# Revit family: Sanaa Basin 45cm PP
name_source: partatom
category: Plumbing Fixtures
units: mm (PartAtom-declared; Revit-internal decimal feet)

## family parameters
Always vertical = Yes
Cut with Voids When Loaded = No
Enable Cutting in Views = No
Maintain Annotation Orientation = No
OmniClass Number = 23.45.05.14.99
OmniClass Title = Other Sanitary Washing Plumbing Fixtures
Part Type = Normal
Room Calculation Point = No
Round Connector Dimension = Use Diameter
Shared = No
Work Plane-Based = No

## types (1)
- Sanaa Basin 45cm PP
    Category = Basins – Wall Hung
    Colour = White
    Default Elevation = 0 mm  [stored 0 ft]
    Fixing Details = Basin Fixing Bolts not supplied, 8mm bolts recommended
    Manufacturer = Lecico SA
    Material = Vitreous China
    Model = Sanaa Basin 45cm PP
    Product code = SANBASWHU0458UE
    Technical dimensions = W458 x H207 x D302mm
    URL = https://www.lecicosa.co.za
    WHB Height = 600 mm

note: [stored X ft] marks values corroborated as IEEE doubles in the binary element streams (Revit-internal decimal feet)

## geometry (parser evidence)
native form markers: Sweep x3
no freeform markers — native parametric forms only
